# Revit family: Контейнерная площадка «Бункер» Арт 13887
name_source: partatom
category: Антураж
revit_build: Autodesk Revit 2018 (Build: 20180423_1000(x64)
units: mm (PartAtom-declared; Revit-internal decimal feet)

## family parameters
Всегда вертикально = Да
Источник визуального образа = Геометрия семейства
На основе рабочей плоскости = Нет
Общий = Нет
При загрузке вырезать с полостями = Нет
Точка расчета площади = Нет

## types (6) — shared parameters
URL = https://hobbyka.ru
Артикул товара = Арт. 13887
Высота = 2500 мм
Группа модели = Контейнерные площадки для ТБО
Изготовитель = ООО «Хоббика»
Материал изделия = Сталь, дерево
Цвет каркаса = Сталь
Цвет отделки = Дерево
Ширина = 2100 мм

## per-type parameters (varying)
| type | Версия 2,8 м | Версия 4,1 м | Версия 5,5 м | Версия 6,9 м | Версия 8,2 м | Версия 9,1 м | Длина | Изображение типоразмера | Описание |
| Версия 2,8 м | Да | Нет | Нет | Нет | Нет | Нет | 2800 мм | Контейнерная площадка «Бункер» Арт 13887 2,8 м.jpg | Контейнерная площадка «Бункер». Версия 2,8 м на 1 контейнер |
| Версия 4,1 м | Нет | Да | Нет | Нет | Нет | Нет | 4100 мм | Контейнерная площадка «Бункер» Арт 13887 4,1 м.jpg | Контейнерная площадка «Бункер». Версия 4,1 м на 2 контейнера |
| Версия 6,9 м | Нет | Нет | Нет | Да | Нет | Нет | 6900 мм | Контейнерная площадка «Бункер» Арт 13887.jpg | Контейнерная площадка «Бункер». Версия 6,9 м на 4 контейнера |
| Версия 8,2 м | Нет | Нет | Нет | Нет | Да | Нет | 8200 мм | Контейнерная площадка «Бункер» Арт 13887.jpg | Контейнерная площадка «Бункер». Версия 8,2 м на 5 контейнеров |
| Версия 9,1 м | Нет | Нет | Нет | Нет | Нет | Да | 9100 мм | Контейнерная площадка «Бункер» Арт 13887.jpg | Контейнерная площадка «Бункер». Версия 9,1 м на 6 контейнеров |
| Версия 5,5 м | Нет | Нет | Да | Нет | Нет | Нет | 5500 мм | Контейнерная площадка «Бункер» Арт 13887 5,5 м.jpg | Контейнерная площадка «Бункер». Версия 5,5 м на 3 контейнера |
